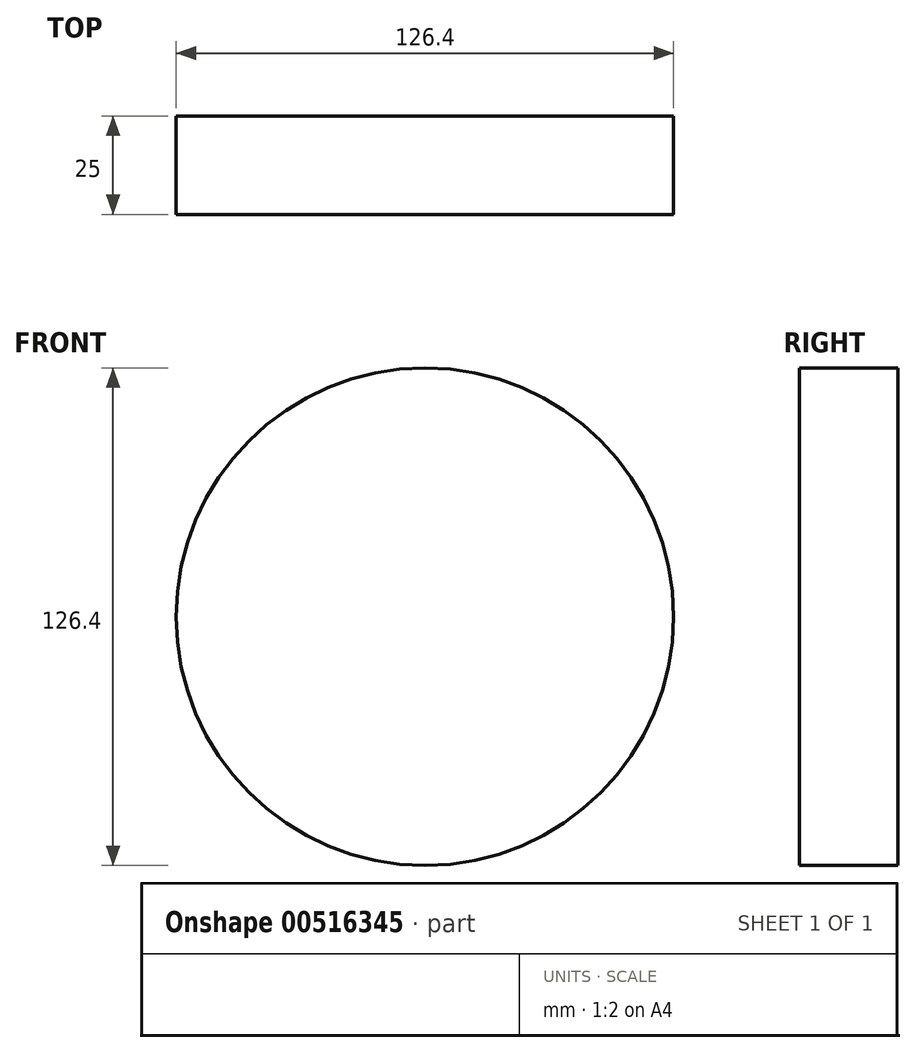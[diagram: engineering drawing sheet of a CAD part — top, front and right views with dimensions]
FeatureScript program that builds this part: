
annotation { "Feature Type Name" : "Feature", "Feature Type Description" : "" }
export const myFeature = defineFeature(function(context is Context, id is Id, definition is map)
    precondition{}
    {
        {
            var Q0;
            Q0=qCreatedBy(makeId("Front.planeOp"),FACE);
            var sketch = newSketch(context, id + "F0", { "sketchPlane" : qUnion([Q0])});
            skCircle(sketch, "E0", {"center": v(0, 0) * mm, "radius": 63.2 * mm});
            skSolve(sketch);
        }
        {
            var Q0;
            Q0 = qSketchRegion(id + "F0", true);
            extrude(context, id + "F1", {"entities" : qUnion([Q0]), "depth" : 25 * mm, "offsetDistance" : 25 * mm});
        }
    });
